# Revit family: Faucet-Lavatory-KOHLER-Triton-K-7401_1
name_source: partatom
category: Plumbing Fixtures
revit_build: Autodesk Revit 2017 (Build: 20160225_1515(x64)
units: mm (PartAtom-declared; Revit-internal decimal feet)

## family parameters
Cut with Voids When Loaded = No
Host = Face
OmniClass Number = 23.31.11.00
OmniClass Title = Faucets
Part Type = Normal
Room Calculation Point = No
Round Connector Dimension = Use Diameter
Shared = No

## types (5) — shared parameters
Assembly Code = D2010
CW Connection = Yes
Cold Water Inlet = Cold Water Inlet
Date Modified = 08/19/2021
Default Elevation = 36"
Drain Included = Yes
Faucet Hole Spacing = 4"
Finish = Kohler-Metal-CP-Polished_Chrome
HW Connection = Yes
Height = 2 5/8"
Hot Water Inlet = Hot Water Inlet
Length = 4"
Manufacturer = KOHLER Co.
Master Format 2014 = 22 41 39
Master Format 2014 Name = Residential Faucets, Supplies, and Trim
Material = Brass Construction
Pressure = 60.00 psi
Product Documentation Link = https://www.us.kohler.com
Product Name = Triton
Product Page URL = http://www.us.kohler.com
Spout Reach = 4"
URL = https://www.us.kohler.com
Vent Connection = No
Waste Connection = No
Waste Water Outlet = Waste Water Outlet
Width = 4"

## per-type parameters (varying)
| type | ADA Compliant | Description | Flow Rate | Handle Clearance | Handle Height | Model | Standard Handle | Type | WaterSense Certified | Without Handle | Wristblade Lever Handle |
| 1.5 GPM, Standard Handle, CP-Polished Chrome | No | Centerset commercial bathroom sink faucet with pop-up drain and standard handles | 2 GPM | 1 1/8" | 2 1/4" | K-7401-2A-CP | Yes | 1 | Yes | No | No |
| 1.5 GPM, Wristblade Lever Handle, CP-Polished Chrome | Yes | Centerset commercial bathroom sink faucet with pop-up drain and wristblade lever handles | 2 GPM | 4" | 4 1/8" | K-7401-5A-CP | No | 2 | Yes | No | Yes |
| 0.5 GPM, Standard Handle, CP-Polished Chrome | No | 0.5 gpm centerset commercial bathroom sink faucet with pop-up drain and standard handles | 1 GPM | 1 1/8" | 2 1/4" | K-7401-2N-CP | Yes | 3 | No | No | No |
| 0.5 GPM, Wristblade Lever Handle, CP-Polished Chrome | Yes | 0.5 gpm centerset commercial bathroom sink faucet with pop-up drain and wristblade lever handles | 1 GPM | 4" | 4 1/8" | K-7401-5N-CP | No | 4 | No | No | Yes |
| 0.5 GPM, Without Handle, CP-Polished Chrome | No | 0.5 gpm centerset commercial bathroom sink base faucet with pop-up drain, requires handles | 1 GPM | 0" | 2" | K-7401-KN-CP | No | 5 | No | Yes | No |

## geometry (parser evidence)
native form markers: Sweep x5
no freeform markers — native parametric forms only
